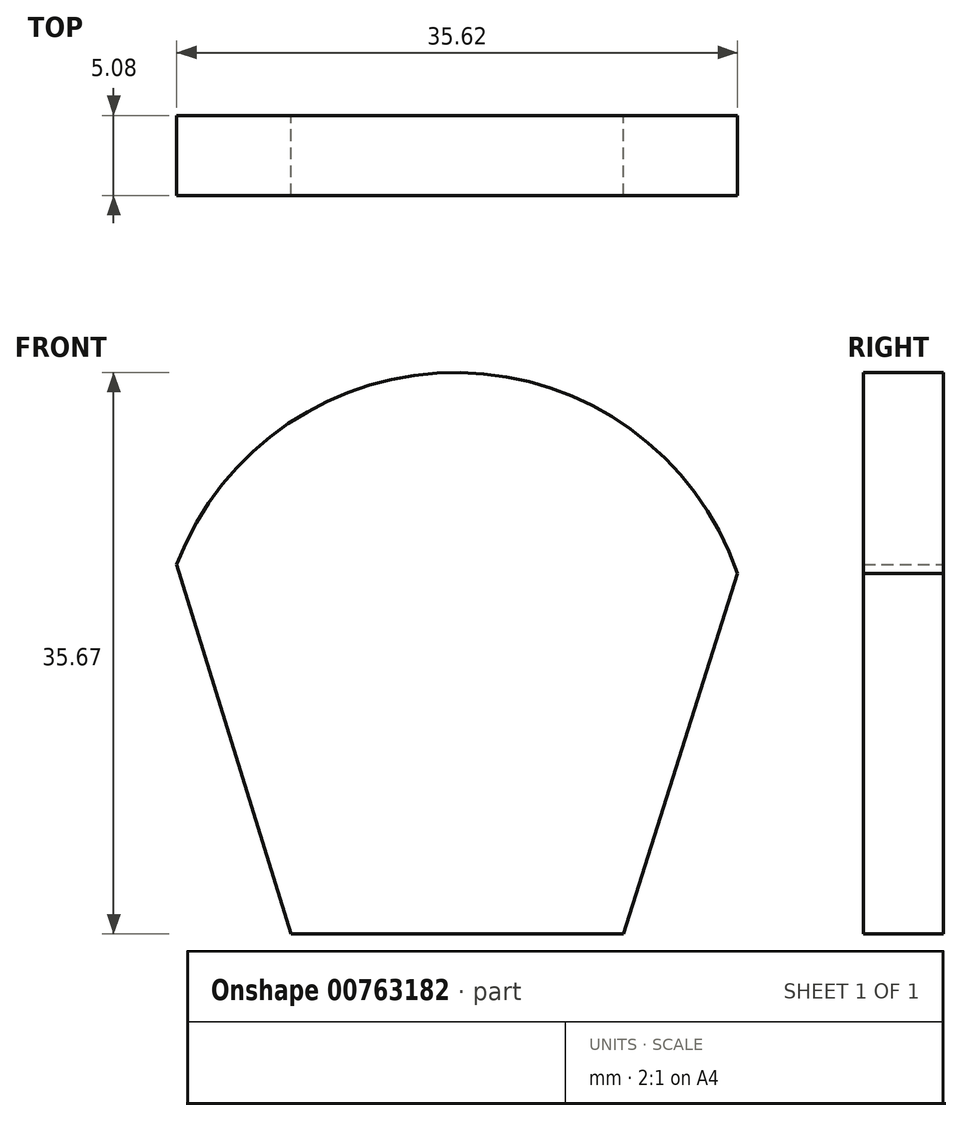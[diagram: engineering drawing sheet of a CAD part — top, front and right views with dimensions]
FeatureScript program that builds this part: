
annotation { "Feature Type Name" : "Feature", "Feature Type Description" : "" }
export const myFeature = defineFeature(function(context is Context, id is Id, definition is map)
    precondition{}
    {
        {
            var Q0;
            Q0=qCreatedBy(makeId("Front.planeOp"),FACE);
            var sketch = newSketch(context, id + "F0", { "sketchPlane" : qUnion([Q0])});
            skLineSegment(sketch, "E0", {"start": v(-19.45, -12.76) * mm, "end": v(1.67, -12.76) * mm});
            skLineSegment(sketch, "E1", {"start": v(-19.45, -12.76) * mm, "end": v(-26.7, 10.72) * mm});
            skLineSegment(sketch, "E2", {"start": v(-19.45, -12.76) * mm, "end": v(-8.9, -12.76) * mm});
            skLineSegment(sketch, "E3.MirrorCS", {"start": v(1.67, -12.76) * mm, "end": v(8.92, 10.16) * mm});
            skArc(sketch, "E4", {"start": v(8.92, 10.16) * mm, "mid": v(-8.7, 22.9) * mm, "end": v(-26.7, 10.72) * mm});
            skSolve(sketch);
        }
        {
            var Q0;
            Q0 = qSketchRegion(id + "F0", true);
            extrude(context, id + "F1", {"entities" : qUnion([Q0]), "depth" : 5.08 * mm, "offsetDistance" : 25.4 * mm});
        }
    });
